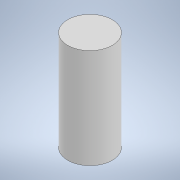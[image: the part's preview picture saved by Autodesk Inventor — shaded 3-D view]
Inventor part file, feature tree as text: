
AUTODESK INVENTOR PART (.ipt)
format: ipt  version: 2020 (Build 240168000, 168)  size: 89,088 bytes
history: native  units: mm
features: extrude x1, sketch x1
ambient origin geometry x8: Origin, YZ Plane, XZ Plane, XY Plane, X Axis, Y Axis, Z Axis, Center Point
bodies: Solide1 (feature_tree)
feature tree (2):
  extrude  "Extrusion1"  Depth=20.0mm
  sketch  "Esquisse1"
